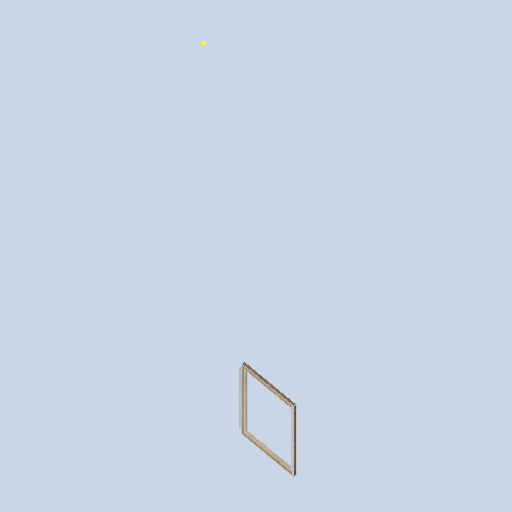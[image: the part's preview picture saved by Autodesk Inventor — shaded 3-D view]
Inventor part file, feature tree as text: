
AUTODESK INVENTOR PART (.ipt)
format: ipt  version: 2024.2 (Build 282272000, 272)  size: 121,856 bytes
history: native  units: in
note: dims shown in document units (in); Inventor stores cm internally (conversion verified against a paired STEP export)
features: sketch x9, plane x4, other x3
ambient origin geometry x8: Origin, YZ Plane, XZ Plane, XY Plane, X Axis, Y Axis, Z Axis, Center Point
bodies: Solid1 (feature_tree)
feature tree (16):
  other  "eave_frame_side.ipt"
  other  "Solid1::eave_frame_side.ipt"
  other  "TaggingFeature1"
  sketch  "Sketch1"  dims[d0=0.3937in]
  sketch  "Sketch2"
  sketch  "Sketch3"
  sketch  "Sketch4"
  sketch  "Sketch5"
  sketch  "Sketch6"
  sketch  "Sketch7"
  sketch  "Sketch8"
  sketch  "Sketch9"
  plane  "Work Plane1"
  plane  "Work Plane2"
  plane  "Work Plane3"
  plane  "Work Plane4"
